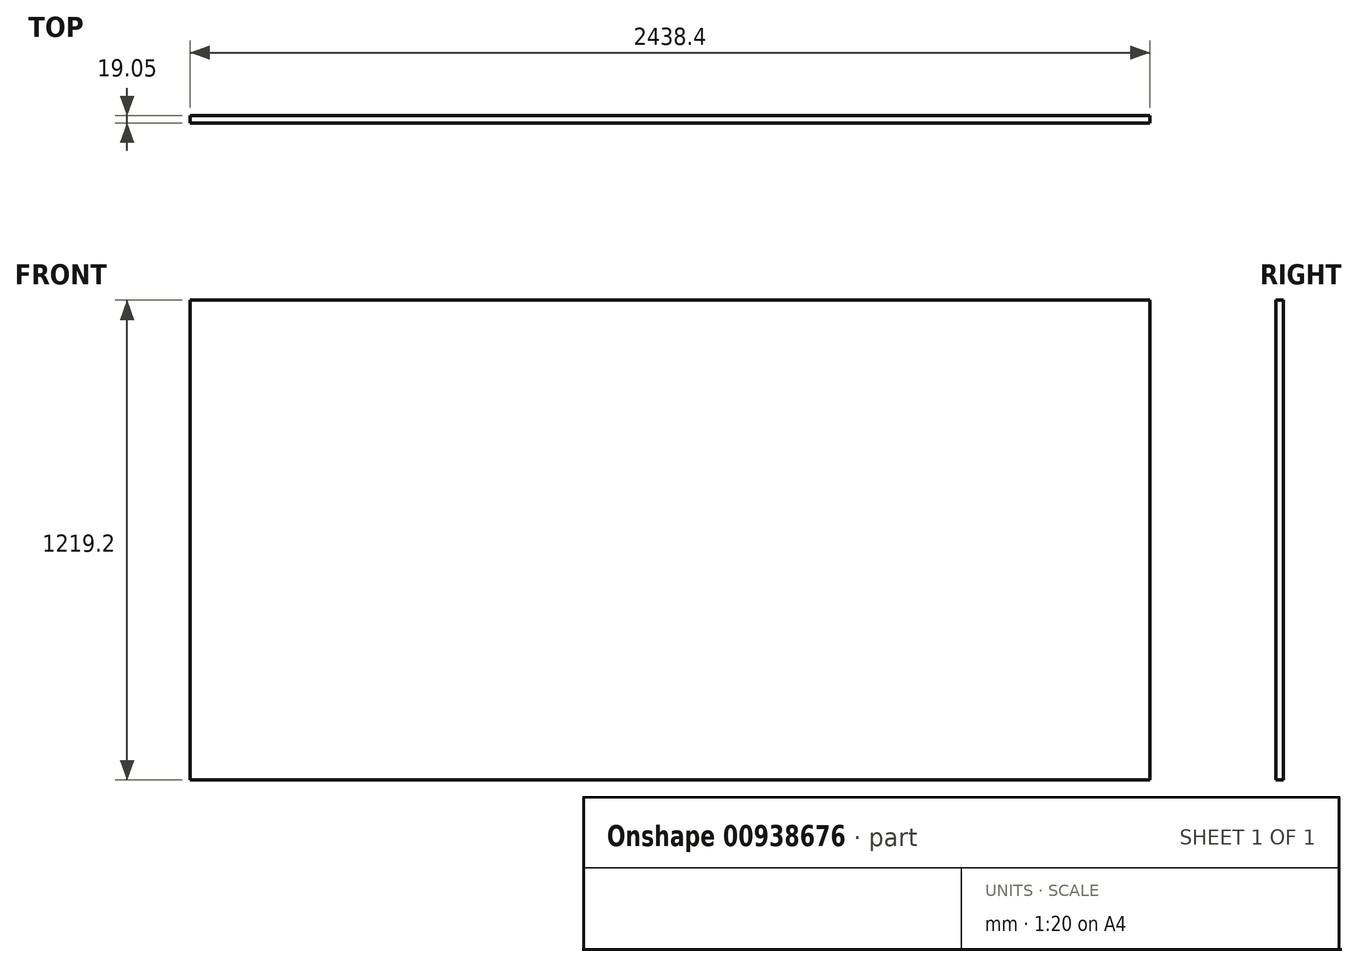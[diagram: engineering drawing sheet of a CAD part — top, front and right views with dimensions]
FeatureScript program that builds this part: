
annotation { "Feature Type Name" : "Feature", "Feature Type Description" : "" }
export const myFeature = defineFeature(function(context is Context, id is Id, definition is map)
    precondition{}
    {
        {
            var Q0;
            Q0=qCreatedBy(makeId("Front.planeOp"),FACE);
            var sketch = newSketch(context, id + "F0", { "sketchPlane" : qUnion([Q0])});
            skLineSegment(sketch, "E0.bottom", {"start": v(1219.2, -609.6) * mm, "end": v(-1219.2, -609.6) * mm});
            skLineSegment(sketch, "E0.top", {"start": v(1219.2, 609.6) * mm, "end": v(-1219.2, 609.6) * mm});
            skLineSegment(sketch, "E0.left", {"start": v(1219.2, -609.6) * mm, "end": v(1219.2, 609.6) * mm});
            skLineSegment(sketch, "E0.right", {"start": v(-1219.2, -609.6) * mm, "end": v(-1219.2, 609.6) * mm});
            skPoint(sketch, "E0.middle", {"position": v(0, 0) * mm});
            skSolve(sketch);
        }
        {
            var Q0;
            Q0=makeQuery(id+"F0.imprint","IMPRINT",FACE,{"disambiguationData":[TD([[makeQuery(id+"F0.imprint","IMPRINT",EDGE,{"derivedFrom":sQuery(id+"F0.wireOp",EDGE,"E0.bottom")}),-1.0]])]});
            var sketch = newSketch(context, id + "F1", { "sketchPlane" : qUnion([Q0])});
            skSolve(sketch);
        }
        {
            var Q0;
            Q0=makeQuery(id+"F1.imprint","IMPRINT",FACE,{"disambiguationData":[TD([[makeQuery(id+"F1.imprint","IMPRINT",EDGE,{"derivedFrom":makeQuery(id+"F0.imprint","IMPRINT",EDGE,{"derivedFrom":sQuery(id+"F0.wireOp",EDGE,"E0.bottom")})}),-1.0]])]});
            extrude(context, id + "F2", {"entities" : qUnion([Q0]), "depth" : 19.05 * mm, "offsetDistance" : 25.4 * mm});
        }
    });
